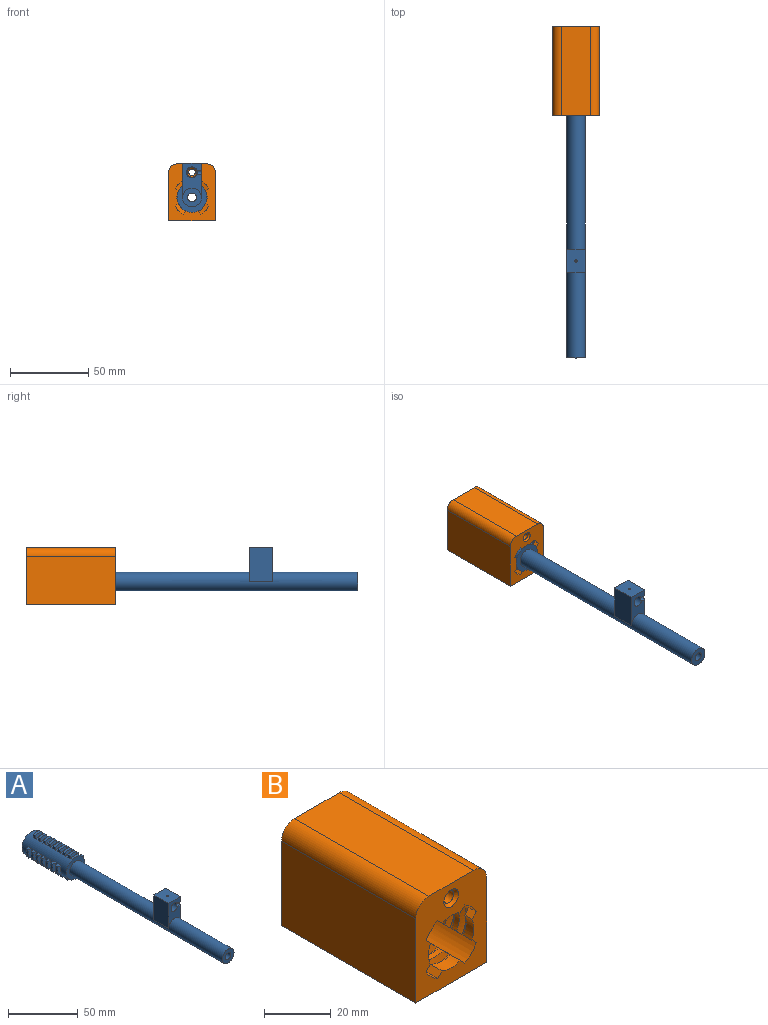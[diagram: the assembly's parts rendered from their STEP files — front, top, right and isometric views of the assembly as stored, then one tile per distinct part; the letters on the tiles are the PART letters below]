
ASSEMBLY  parts=2 mates=1
PART A: 166 faces, bbox 27.8x200.1x34.1 mm
  f0: cylinder r=9.5mm len=45mm, axis (0,1,0), area 2062.4mm2, adj f1,f2,f11,f12,f14,f15,f16,f17
  f1: plane 19x19mm, normal (0,1,0), area 169.7mm2, adj f0,f10
  f2: plane 19x19mm, normal (0,-1,0), area 170.4mm2, adj f0,f3
  f3: cylinder r=6mm len=155mm, axis (0,1,0), area 5560.6mm2, adj f2,f4,f156,f157,f160,f161
  f4: plane 12x12mm, normal (0,-1,0), area 87.6mm2, adj f3,f5
  f5: cylinder r=2.85mm len=157.2mm, axis (0,1,0), area 2815mm2, adj f4,f6
  f6: plane 6.43x6.43mm, normal (0,1,0), area 7mm2, adj f5,f7
  f7: cylinder r=3.21mm len=6.43mm, axis (0,1,0), area 104mm2, adj f6,f8
  f8: cone r=3.21mm half-angle=23deg, axis (0,1,0), area 79.8mm2, adj f7,f9
  f9: cone r=4.5mm half-angle=0.5deg, axis (0,1,0), area 974.5mm2, adj f8,f10
  f10: cone r=4.79mm half-angle=45deg, axis (0,1,0), area 59.1mm2, adj f1,f9
  f11: bspline ~20.78x7.25mm, area 18.4mm2, adj f0,f13,f14,f15
  f12: bspline ~20.78x7.25mm, area 18.4mm2, adj f0,f13,f14,f15
  f13: cylinder r=12mm len=7mm, axis (0,-1,0), area 14.2mm2, adj f11,f12,f14,f15
  f14: plane 3.1x2.75mm, normal (-1,0,0), area 6.6mm2, adj f0,f11,f12,f13
  f15: plane 3.1x2.75mm, normal (1,0,0), area 6.6mm2, adj f0,f11,f12,f13
  f16: bspline ~20.78x7.25mm, area 18.4mm2, adj f0,f18,f19,f20
  f17: bspline ~20.78x7.25mm, area 18.4mm2, adj f0,f18,f19,f20
  f18: cylinder r=12mm len=7mm, axis (0,-1,0), area 14.2mm2, adj f16,f17,f19,f20
  f19: plane 3.1x2.75mm, normal (-1,0,0), area 6.6mm2, adj f0,f16,f17,f18
  f20: plane 3.1x2.75mm, normal (1,0,0), area 6.6mm2, adj f0,f16,f17,f18
  f21: bspline ~20.78x7.25mm, area 18.4mm2, adj f0,f23,f24,f25
  f22: bspline ~20.78x7.25mm, area 18.4mm2, adj f0,f23,f24,f25
  f23: cylinder r=12mm len=7mm, axis (0,-1,0), area 14.2mm2, adj f21,f22,f24,f25
  f24: plane 3.1x2.75mm, normal (-1,0,0), area 6.6mm2, adj f0,f21,f22,f23
  f25: plane 3.1x2.75mm, normal (1,0,0), area 6.6mm2, adj f0,f21,f22,f23
  f26: bspline ~20.78x7.25mm, area 18.4mm2, adj f0,f28,f29,f30
  f27: bspline ~20.78x7.25mm, area 18.4mm2, adj f0,f28,f29,f30
  f28: cylinder r=12mm len=7mm, axis (0,-1,0), area 14.2mm2, adj f26,f27,f29,f30
  f29: plane 3.1x2.75mm, normal (-1,0,0), area 6.6mm2, adj f0,f26,f27,f28
  f30: plane 3.1x2.75mm, normal (1,0,0), area 6.6mm2, adj f0,f26,f27,f28
  f31: bspline ~20.78x7.25mm, area 18.4mm2, adj f0,f33,f34,f35
  f32: bspline ~20.78x7.25mm, area 18.4mm2, adj f0,f33,f34,f35
  f33: cylinder r=12mm len=7mm, axis (0,-1,0), area 14.2mm2, adj f31,f32,f34,f35
  f34: plane 3.1x2.75mm, normal (-1,0,0), area 6.6mm2, adj f0,f31,f32,f33
  f35: plane 3.1x2.75mm, normal (1,0,0), area 6.6mm2, adj f0,f31,f32,f33
  f36: bspline ~20.78x7.25mm, area 18.4mm2, adj f0,f38,f39,f40
  f37: bspline ~20.78x7.25mm, area 18.4mm2, adj f0,f38,f39,f40
  f38: cylinder r=12mm len=7mm, axis (0,-1,0), area 14.2mm2, adj f36,f37,f39,f40
  f39: plane 3.1x2.75mm, normal (-1,0,0), area 6.6mm2, adj f0,f36,f37,f38
  f40: plane 3.1x2.75mm, normal (1,0,0), area 6.6mm2, adj f0,f36,f37,f38
  f41: bspline ~20.78x7.25mm, area 18.4mm2, adj f0,f43,f44,f45
  f42: bspline ~20.78x7.25mm, area 18.4mm2, adj f0,f43,f44,f45
  f43: cylinder r=12mm len=7mm, axis (0,-1,0), area 14.2mm2, adj f41,f42,f44,f45
  f44: plane 3.1x2.75mm, normal (-1,0,0), area 6.6mm2, adj f0,f41,f42,f43
  f45: plane 3.1x2.75mm, normal (1,0,0), area 6.6mm2, adj f0,f41,f42,f43
  f46: bspline ~20.78x7.25mm, area 18.4mm2, adj f0,f48,f49,f50
  f47: bspline ~20.78x7.25mm, area 18.4mm2, adj f0,f48,f49,f50
  f48: cylinder r=12mm len=7mm, axis (0,-1,0), area 14.2mm2, adj f46,f47,f49,f50
  f49: plane 3.1x2.75mm, normal (-1,0,0), area 6.6mm2, adj f0,f46,f47,f48
  f50: plane 3.1x2.75mm, normal (1,0,0), area 6.6mm2, adj f0,f46,f47,f48
  f51: bspline ~20.78x7.25mm, area 18.4mm2, adj f0,f53,f54,f55
  f52: bspline ~20.78x7.25mm, area 18.4mm2, adj f0,f53,f54,f55
  f53: cylinder r=12mm len=7mm, axis (0,-1,0), area 14.2mm2, adj f51,f52,f54,f55
  f54: plane 3.1x2.75mm, normal (-1,0,0), area 6.6mm2, adj f0,f51,f52,f53
  f55: plane 3.1x2.75mm, normal (1,0,0), area 6.6mm2, adj f0,f51,f52,f53
  f56: bspline ~20.78x7.25mm, area 18.4mm2, adj f0,f58,f59,f60
  f57: bspline ~20.78x7.25mm, area 18.4mm2, adj f0,f58,f59,f60
  f58: cylinder r=12mm len=7mm, axis (0,-1,0), area 14.2mm2, adj f56,f57,f59,f60
  f59: plane 3.1x2.75mm, normal (-1,0,0), area 6.6mm2, adj f0,f56,f57,f58
  f60: plane 3.1x2.75mm, normal (1,0,0), area 6.6mm2, adj f0,f56,f57,f58
  f61: bspline ~20.78x7.25mm, area 18.4mm2, adj f0,f63,f64,f65
  f62: bspline ~20.78x7.25mm, area 18.4mm2, adj f0,f63,f64,f65
  f63: cylinder r=12mm len=7mm, axis (0,-1,0), area 14.2mm2, adj f61,f62,f64,f65
  f64: plane 3.1x2.75mm, normal (-1,0,0), area 6.6mm2, adj f0,f61,f62,f63
  f65: plane 3.1x2.75mm, normal (1,0,0), area 6.6mm2, adj f0,f61,f62,f63
  f66: bspline ~12x5.63mm, area 18.4mm2, adj f0,f68,f69,f70
  f67: bspline ~12x5.63mm, area 18.4mm2, adj f0,f68,f69,f70
  f68: cylinder r=12mm len=7mm, axis (0,-1,0), area 14.2mm2, adj f66,f67,f69,f70
  f69: plane 3.11x2.75mm, normal (0,0,-1), area 6.6mm2, adj f0,f66,f67,f68
  f70: plane 3.11x2.75mm, normal (0,0,1), area 6.6mm2, adj f0,f66,f67,f68
  f71: bspline ~20.78x7.25mm, area 18.4mm2, adj f0,f73,f74,f75
  f72: bspline ~20.78x7.25mm, area 18.4mm2, adj f0,f73,f74,f75
  f73: cylinder r=12mm len=7mm, axis (0,-1,0), area 14.2mm2, adj f71,f72,f74,f75
  f74: plane 3.1x2.75mm, normal (-1,0,0), area 6.6mm2, adj f0,f71,f72,f73
  f75: plane 3.1x2.75mm, normal (1,0,0), area 6.6mm2, adj f0,f71,f72,f73
  f76: bspline ~20.78x7.25mm, area 18.4mm2, adj f0,f78,f79,f80
  f77: bspline ~20.78x7.25mm, area 18.4mm2, adj f0,f78,f79,f80
  f78: cylinder r=12mm len=7mm, axis (0,-1,0), area 14.2mm2, adj f76,f77,f79,f80
  f79: plane 3.1x2.75mm, normal (-1,0,0), area 6.6mm2, adj f0,f76,f77,f78
  f80: plane 3.1x2.75mm, normal (1,0,0), area 6.6mm2, adj f0,f76,f77,f78
  f81: bspline ~12x5.63mm, area 18.4mm2, adj f0,f83,f84,f85
  f82: bspline ~12x5.63mm, area 18.4mm2, adj f0,f83,f84,f85
  f83: cylinder r=12mm len=7mm, axis (0,-1,0), area 14.2mm2, adj f81,f82,f84,f85
  f84: plane 3.11x2.75mm, normal (0,0,-1), area 6.6mm2, adj f0,f81,f82,f83
  f85: plane 3.11x2.75mm, normal (0,0,1), area 6.6mm2, adj f0,f81,f82,f83
  f86: bspline ~20.78x7.25mm, area 18.4mm2, adj f0,f88,f89,f90
  f87: bspline ~20.78x7.25mm, area 18.4mm2, adj f0,f88,f89,f90
  f88: cylinder r=12mm len=7mm, axis (0,-1,0), area 14.2mm2, adj f86,f87,f89,f90
  f89: plane 3.1x2.75mm, normal (-1,0,0), area 6.6mm2, adj f0,f86,f87,f88
  f90: plane 3.1x2.75mm, normal (1,0,0), area 6.6mm2, adj f0,f86,f87,f88
  f91: bspline ~12x5.63mm, area 18.4mm2, adj f0,f93,f94,f95
  f92: bspline ~12x5.63mm, area 18.4mm2, adj f0,f93,f94,f95
  f93: cylinder r=12mm len=7mm, axis (0,-1,0), area 14.2mm2, adj f91,f92,f94,f95
  f94: plane 3.11x2.75mm, normal (0,0,-1), area 6.6mm2, adj f0,f91,f92,f93
  f95: plane 3.11x2.75mm, normal (0,0,1), area 6.6mm2, adj f0,f91,f92,f93
  f96: bspline ~20.78x7.25mm, area 18.4mm2, adj f0,f98,f99,f100
  f97: bspline ~20.78x7.25mm, area 18.4mm2, adj f0,f98,f99,f100
  f98: cylinder r=12mm len=7mm, axis (0,-1,0), area 14.2mm2, adj f96,f97,f99,f100
  f99: plane 3.1x2.75mm, normal (-1,0,0), area 6.6mm2, adj f0,f96,f97,f98
  f100: plane 3.1x2.75mm, normal (1,0,0), area 6.6mm2, adj f0,f96,f97,f98
  f101: bspline ~12x5.63mm, area 18.4mm2, adj f0,f103,f104,f105
  f102: bspline ~12x5.63mm, area 18.4mm2, adj f0,f103,f104,f105
  f103: cylinder r=12mm len=7mm, axis (0,-1,0), area 14.2mm2, adj f101,f102,f104,f105
  f104: plane 3.11x2.75mm, normal (0,0,-1), area 6.6mm2, adj f0,f101,f102,f103
  f105: plane 3.11x2.75mm, normal (0,0,1), area 6.6mm2, adj f0,f101,f102,f103
  f106: bspline ~12x5.63mm, area 18.4mm2, adj f0,f108,f109,f110
  f107: bspline ~12x5.63mm, area 18.4mm2, adj f0,f108,f109,f110
  f108: cylinder r=12mm len=7mm, axis (0,-1,0), area 14.2mm2, adj f106,f107,f109,f110
  f109: plane 3.11x2.75mm, normal (0,0,-1), area 6.6mm2, adj f0,f106,f107,f108
  f110: plane 3.11x2.75mm, normal (0,0,1), area 6.6mm2, adj f0,f106,f107,f108
  f111: bspline ~12x5.63mm, area 18.4mm2, adj f0,f113,f114,f115
  f112: bspline ~12x5.63mm, area 18.4mm2, adj f0,f113,f114,f115
  f113: cylinder r=12mm len=7mm, axis (0,-1,0), area 14.2mm2, adj f111,f112,f114,f115
  f114: plane 3.11x2.75mm, normal (0,0,-1), area 6.6mm2, adj f0,f111,f112,f113
  f115: plane 3.11x2.75mm, normal (0,0,1), area 6.6mm2, adj f0,f111,f112,f113
  f116: bspline ~12x5.63mm, area 18.4mm2, adj f0,f118,f119,f120
  f117: bspline ~12x5.63mm, area 18.4mm2, adj f0,f118,f119,f120
  f118: cylinder r=12mm len=7mm, axis (0,-1,0), area 14.2mm2, adj f116,f117,f119,f120
  f119: plane 3.11x2.75mm, normal (0,0,-1), area 6.6mm2, adj f0,f116,f117,f118
  f120: plane 3.11x2.75mm, normal (0,0,1), area 6.6mm2, adj f0,f116,f117,f118
  f121: bspline ~12x5.63mm, area 18.4mm2, adj f0,f123,f124,f125
  f122: bspline ~12x5.63mm, area 18.4mm2, adj f0,f123,f124,f125
  f123: cylinder r=12mm len=7mm, axis (0,-1,0), area 14.2mm2, adj f121,f122,f124,f125
  f124: plane 3.11x2.75mm, normal (0,0,1), area 6.6mm2, adj f0,f121,f122,f123
  f125: plane 3.11x2.75mm, normal (0,0,-1), area 6.6mm2, adj f0,f121,f122,f123
  f126: bspline ~12x5.63mm, area 18.4mm2, adj f0,f128,f129,f130
  f127: bspline ~12x5.63mm, area 18.4mm2, adj f0,f128,f129,f130
  f128: cylinder r=12mm len=7mm, axis (0,-1,0), area 14.2mm2, adj f126,f127,f129,f130
  f129: plane 3.11x2.75mm, normal (0,0,1), area 6.6mm2, adj f0,f126,f127,f128
  f130: plane 3.11x2.75mm, normal (0,0,-1), area 6.6mm2, adj f0,f126,f127,f128
  f131: bspline ~12x5.63mm, area 18.4mm2, adj f0,f133,f134,f135
  f132: bspline ~12x5.63mm, area 18.4mm2, adj f0,f133,f134,f135
  f133: cylinder r=12mm len=7mm, axis (0,-1,0), area 14.2mm2, adj f131,f132,f134,f135
  f134: plane 3.11x2.75mm, normal (0,0,1), area 6.6mm2, adj f0,f131,f132,f133
  f135: plane 3.11x2.75mm, normal (0,0,-1), area 6.6mm2, adj f0,f131,f132,f133
  f136: bspline ~12x5.63mm, area 18.4mm2, adj f0,f138,f139,f140
  f137: bspline ~12x5.63mm, area 18.4mm2, adj f0,f138,f139,f140
  f138: cylinder r=12mm len=7mm, axis (0,-1,0), area 14.2mm2, adj f136,f137,f139,f140
  f139: plane 3.11x2.75mm, normal (0,0,1), area 6.6mm2, adj f0,f136,f137,f138
  f140: plane 3.11x2.75mm, normal (0,0,-1), area 6.6mm2, adj f0,f136,f137,f138
  f141: bspline ~12x5.63mm, area 18.4mm2, adj f0,f143,f144,f145
  f142: bspline ~12x5.63mm, area 18.4mm2, adj f0,f143,f144,f145
  f143: cylinder r=12mm len=7mm, axis (0,-1,0), area 14.2mm2, adj f141,f142,f144,f145
  f144: plane 3.11x2.75mm, normal (0,0,1), area 6.6mm2, adj f0,f141,f142,f143
  f145: plane 3.11x2.75mm, normal (0,0,-1), area 6.6mm2, adj f0,f141,f142,f143
  f146: bspline ~12x5.63mm, area 18.4mm2, adj f0,f148,f149,f150
  f147: bspline ~12x5.63mm, area 18.4mm2, adj f0,f148,f149,f150
  f148: cylinder r=12mm len=7mm, axis (0,-1,0), area 14.2mm2, adj f146,f147,f149,f150
  f149: plane 3.11x2.75mm, normal (0,0,1), area 6.6mm2, adj f0,f146,f147,f148
  f150: plane 3.11x2.75mm, normal (0,0,-1), area 6.6mm2, adj f0,f146,f147,f148
  f151: bspline ~12x5.63mm, area 18.4mm2, adj f0,f153,f154,f155
  f152: bspline ~12x5.63mm, area 18.4mm2, adj f0,f153,f154,f155
  f153: cylinder r=12mm len=7mm, axis (0,-1,0), area 14.2mm2, adj f151,f152,f154,f155
  f154: plane 3.11x2.75mm, normal (0,0,1), area 6.6mm2, adj f0,f151,f152,f153
  f155: plane 3.11x2.75mm, normal (0,0,-1), area 6.6mm2, adj f0,f151,f152,f153
  f156: plane 22x15mm, normal (-1,0,0), area 330mm2, adj f3,f158,f160,f161
  f157: plane 22x15mm, normal (1,0,0), area 326.5mm2, adj f3,f158,f160,f161,f165
  f158: plane 15x12mm, normal (0,0,1), area 178.2mm2, adj f156,f157,f160,f161,f162
  f159: cylinder r=3.5mm len=15mm, axis (0,-1,0), area 322.7mm2, adj f160,f161,f162,f163,f165
  f160: plane 22x12mm, normal (0,1,0), area 169mm2, adj f3,f156,f157,f158,f159
  f161: plane 22x12mm, normal (0,-1,0), area 161.1mm2, adj f3,f156,f157,f158,f159,f165
  f162: cylinder r=0.75mm len=2.58mm, axis (0,0,1), area 12.2mm2, adj f158,f159
  f163: cylinder r=0.75mm len=6.58mm, axis (0,0,1), area 30.7mm2, adj f159,f164
  f164: plane 1.5x1.5mm, normal (0,0,1), area 1.8mm2, adj f163
  f165: cylinder r=1.5mm len=3mm, axis (1,0,0), area 12.6mm2, adj f157,f159,f161
PART B: 198 faces, bbox 30.3x57.3x36.8 mm
  f0: bspline ~20.96x7.35mm, area 25.1mm2, adj f72,f101,f119,f167
  f1: bspline ~20.96x7.35mm, area 25.1mm2, adj f72,f99,f118,f168
  f2: bspline ~20.96x7.35mm, area 25.1mm2, adj f72,f106,f114,f170
  f3: bspline ~20.96x7.35mm, area 25.1mm2, adj f72,f103,f112,f171
  f4: bspline ~20.96x7.35mm, area 25.1mm2, adj f72,f85,f129,f158
  f5: bspline ~20.96x7.35mm, area 25.1mm2, adj f72,f83,f127,f160
  f6: bspline ~20.96x7.35mm, area 25.1mm2, adj f72,f90,f123,f164
  f7: bspline ~20.96x7.35mm, area 25.1mm2, adj f72,f91,f121,f166
  f8: bspline ~12.1x5.74mm, area 25.1mm2, adj f72,f78,f105,f174
  f9: bspline ~12.1x5.74mm, area 25.1mm2, adj f72,f88,f104,f175
  f10: bspline ~12.1x5.74mm, area 25.1mm2, adj f72,f86,f102,f176
  f11: bspline ~12.1x5.74mm, area 25.1mm2, adj f72,f84,f100,f177
  f12: bspline ~20.96x7.35mm, area 25.1mm2, adj f72,f97,f110,f172
  f13: bspline ~20.96x7.35mm, area 25.1mm2, adj f72,f95,f108,f173
  f14: bspline ~12.1x5.74mm, area 25.1mm2, adj f72,f84,f100,f177
  f15: bspline ~12.1x5.74mm, area 25.1mm2, adj f72,f82,f98,f178
  f16: bspline ~20.96x7.35mm, area 25.1mm2, adj f72,f95,f108,f173
  f17: bspline ~20.96x7.35mm, area 25.1mm2, adj f72,f93,f116,f169
  f18: bspline ~20.96x7.35mm, area 25.1mm2, adj f72,f87,f131,f156
  f19: bspline ~20.96x7.35mm, area 25.1mm2, adj f72,f85,f129,f158
  f20: bspline ~20.96x7.35mm, area 25.1mm2, adj f72,f75,f76,f150
  f21: bspline ~20.96x7.35mm, area 25.1mm2, adj f72,f106,f114,f170
  f22: bspline ~20.96x7.35mm, area 25.1mm2, adj f72,f89,f134,f153
  f23: bspline ~20.96x7.35mm, area 25.1mm2, adj f72,f87,f131,f156
  f24: bspline ~12.1x5.74mm, area 25.1mm2, adj f72,f75,f77,f150
  f25: bspline ~12.1x5.74mm, area 25.1mm2, adj f72,f78,f105,f174
  f26: bspline ~20.96x7.35mm, area 25.1mm2, adj f72,f74,f79,f150,f151
  f27: bspline ~20.96x7.35mm, area 25.1mm2, adj f72,f89,f134,f153
  f28: bspline ~20.96x7.35mm, area 25.1mm2, adj f72,f81,f125,f162
  f29: bspline ~20.96x7.35mm, area 25.1mm2, adj f72,f90,f123,f164
  f30: bspline ~20.96x7.35mm, area 25.1mm2, adj f72,f73,f77,f150
  f31: bspline ~11.43x3.64mm, area 25.1mm2, adj f72,f73,f79,f150,f151
  f32: bspline ~20.96x7.35mm, area 25.1mm2, adj f72,f103,f112,f171
  f33: bspline ~20.96x7.35mm, area 25.1mm2, adj f72,f101,f119,f167
  f34: bspline ~12.1x5.74mm, area 25.1mm2, adj f72,f88,f104,f175
  f35: bspline ~12.1x5.74mm, area 25.1mm2, adj f72,f86,f102,f176
  f36: bspline ~12.1x5.74mm, area 25.1mm2, adj f72,f80,f96,f179
  f37: bspline ~12.1x5.74mm, area 25.1mm2, adj f72,f92,f94,f180
  f38: bspline ~12.1x5.74mm, area 25.1mm2, adj f72,f82,f98,f178
  f39: bspline ~12.1x5.74mm, area 25.1mm2, adj f72,f80,f96,f179
  f40: bspline ~20.96x7.35mm, area 25.1mm2, adj f72,f83,f127,f160
  f41: bspline ~20.96x7.35mm, area 25.1mm2, adj f72,f81,f125,f162
  f42: bspline ~20.96x7.35mm, area 25.1mm2, adj f72,f99,f118,f168
  f43: bspline ~20.96x7.35mm, area 25.1mm2, adj f72,f97,f110,f172
  f44: bspline ~12.1x5.74mm, area 25.1mm2, adj f72,f113,f133,f154
  f45: bspline ~12.1x5.74mm, area 25.1mm2, adj f72,f111,f132,f155
  f46: bspline ~12.1x5.74mm, area 25.1mm2, adj f72,f107,f124,f163
  f47: bspline ~12.1x5.74mm, area 25.1mm2, adj f72,f115,f122,f165
  f48: bspline ~12.1x5.74mm, area 25.1mm2, adj f72,f109,f126,f161
  f49: bspline ~12.1x5.74mm, area 25.1mm2, adj f72,f107,f124,f163
  f50: bspline ~12.1x5.74mm, area 25.1mm2, adj f72,f117,f128,f159
  f51: bspline ~12.1x5.74mm, area 25.1mm2, adj f72,f109,f126,f161
  f52: bspline ~12.1x5.74mm, area 25.1mm2, adj f72,f120,f130,f157
  f53: bspline ~12.1x5.74mm, area 25.1mm2, adj f72,f117,f128,f159
  f54: bspline ~12.1x5.74mm, area 25.1mm2, adj f72,f111,f132,f155
  f55: bspline ~12.1x5.74mm, area 25.1mm2, adj f72,f120,f130,f157
  f56: bspline ~12.1x5.74mm, area 25.1mm2, adj f72,f74,f76,f150
  f57: bspline ~12.1x5.74mm, area 25.1mm2, adj f72,f113,f133,f154
  f58: plane 36.5x30mm, normal (0,1,0), area 799.2mm2, adj f67,f68,f69,f70,f135,f136,f137,f138
  f59: plane 5.46x3.28mm, normal (0,-1,0), area 13.4mm2, adj f147,f150,f152,f187
  f60: plane 5.06x5.06mm, normal (0,-1,0), area 13.4mm2, adj f145,f148,f150,f188
  f61: plane 5.46x3.28mm, normal (0,-1,0), area 13.4mm2, adj f143,f146,f150,f181
  f62: plane 5.06x5.06mm, normal (0,-1,0), area 13.4mm2, adj f142,f144,f150,f182
  f63: plane 5.46x3.28mm, normal (0,-1,0), area 13.4mm2, adj f139,f141,f150,f183
  f64: plane 5.06x5.06mm, normal (0,-1,0), area 13.4mm2, adj f138,f140,f150,f184
  f65: plane 5.46x3.28mm, normal (0,-1,0), area 13.4mm2, adj f135,f137,f150,f185
  f66: plane 5.06x5.06mm, normal (0,-1,0), area 13.4mm2, adj f136,f149,f150,f186
  f67: plane 57x31mm, normal (1,0,0), area 1767mm2, adj f58,f70,f71,f193
  f68: plane 57x19mm, normal (0,0,1), area 1083mm2, adj f58,f71,f193,f194
  f69: plane 57x31mm, normal (-1,0,0), area 1767mm2, adj f58,f70,f71,f194
  f70: plane 57x30mm, normal (0,0,-1), area 1710mm2, adj f58,f67,f69,f71
  f71: plane 36.5x30mm, normal (0,-1,0), area 691mm2, adj f67,f68,f69,f70,f72,f91,f92,f93
  f72: cylinder r=12.1mm len=39.89mm, axis (0,-1,0), area 1741.4mm2, adj f0,f1,f2,f3,f4,f5,f6,f7
  f73: plane 3.06x1.97mm, normal (-0.71,0,0.71), area 6.6mm2, adj f30,f31,f72,f150
  f74: bspline ~17.79x14.94mm, area 18.4mm2, adj f26,f56,f72,f150
  f75: bspline ~17.79x14.94mm, area 18.4mm2, adj f20,f24,f72,f150
  f76: bspline ~18.96x13.92mm, area 18.4mm2, adj f20,f56,f72,f150
  f77: bspline ~18.96x13.92mm, area 18.4mm2, adj f24,f30,f72,f150
  f78: plane 3.29x2.16mm, normal (0.71,0,0.71), area 6.7mm2, adj f8,f25,f72,f174
  f79: plane 3.17x2.04mm, normal (-0.71,0,-0.71), area 6.6mm2, adj f26,f31,f72,f151
  f80: plane 3.29x2.16mm, normal (0.71,0,0.71), area 6.7mm2, adj f36,f39,f72,f179
  f81: plane 3.17x2.04mm, normal (-0.71,0,-0.71), area 6.6mm2, adj f28,f41,f72,f162
  f82: plane 3.29x2.16mm, normal (0.71,0,0.71), area 6.7mm2, adj f15,f38,f72,f178
  f83: plane 3.17x2.04mm, normal (-0.71,0,-0.71), area 6.6mm2, adj f5,f40,f72,f160
  f84: plane 3.29x2.16mm, normal (0.71,0,0.71), area 6.7mm2, adj f11,f14,f72,f177
  f85: plane 3.17x2.04mm, normal (-0.71,0,-0.71), area 6.6mm2, adj f4,f19,f72,f158
  f86: plane 3.29x2.16mm, normal (0.71,0,0.71), area 6.7mm2, adj f10,f35,f72,f176
  f87: plane 3.17x2.04mm, normal (-0.71,0,-0.71), area 6.6mm2, adj f18,f23,f72,f156
  f88: plane 3.29x2.16mm, normal (0.71,0,0.71), area 6.7mm2, adj f9,f34,f72,f175
  f89: plane 3.17x2.04mm, normal (-0.71,0,-0.71), area 6.6mm2, adj f22,f27,f72,f153
  f90: plane 3.17x2.04mm, normal (-0.71,0,-0.71), area 6.7mm2, adj f6,f29,f72,f164
  f91: plane 2.21x1.97mm, normal (-0.71,0,-0.71), area 5mm2, adj f7,f71,f72,f166
  f92: plane 6.74x1.97mm, normal (0.71,0,0.71), area 16.9mm2, adj f37,f71,f72,f180
  f93: plane 5.5x1.97mm, normal (-0.71,0,0.71), area 13.5mm2, adj f17,f71,f72,f169
  f94: plane 6.02x2.03mm, normal (0.71,0,-0.71), area 14.9mm2, adj f37,f71,f72,f180
  f95: plane 3.16x2.03mm, normal (-0.71,0,0.71), area 6.6mm2, adj f13,f16,f72,f173
  f96: plane 3.17x2.03mm, normal (0.71,0,-0.71), area 6.6mm2, adj f36,f39,f72,f179
  f97: plane 3.16x2.03mm, normal (-0.71,0,0.71), area 6.6mm2, adj f12,f43,f72,f172
  f98: plane 3.17x2.03mm, normal (0.71,0,-0.71), area 6.6mm2, adj f15,f38,f72,f178
  f99: plane 3.16x2.03mm, normal (-0.71,0,0.71), area 6.6mm2, adj f1,f42,f72,f168
  f100: plane 3.17x2.03mm, normal (0.71,0,-0.71), area 6.6mm2, adj f11,f14,f72,f177
  f101: plane 3.16x2.03mm, normal (-0.71,0,0.71), area 6.6mm2, adj f0,f33,f72,f167
  f102: plane 3.17x2.03mm, normal (0.71,0,-0.71), area 6.6mm2, adj f10,f35,f72,f176
  f103: plane 3.16x2.03mm, normal (-0.71,0,0.71), area 6.6mm2, adj f3,f32,f72,f171
  f104: plane 3.17x2.03mm, normal (0.71,0,-0.71), area 6.6mm2, adj f9,f34,f72,f175
  f105: plane 3.17x2.03mm, normal (0.71,0,-0.71), area 6.6mm2, adj f8,f25,f72,f174
  f106: plane 3.16x2.03mm, normal (-0.71,0,0.71), area 6.6mm2, adj f2,f21,f72,f170
  f107: plane 3.29x2.16mm, normal (-0.71,0,-0.71), area 6.7mm2, adj f46,f49,f72,f163
  f108: plane 3.17x2.04mm, normal (0.71,0,0.71), area 6.6mm2, adj f13,f16,f72,f173
  f109: plane 3.29x2.16mm, normal (-0.71,0,-0.71), area 6.7mm2, adj f48,f51,f72,f161
  f110: plane 3.17x2.04mm, normal (0.71,0,0.71), area 6.6mm2, adj f12,f43,f72,f172
  f111: plane 3.29x2.16mm, normal (-0.71,0,-0.71), area 6.7mm2, adj f45,f54,f72,f155
  f112: plane 3.17x2.04mm, normal (0.71,0,0.71), area 6.6mm2, adj f3,f32,f72,f171
  f113: plane 3.29x2.16mm, normal (-0.71,0,-0.71), area 6.7mm2, adj f44,f57,f72,f154
  f114: plane 3.17x2.04mm, normal (0.71,0,0.71), area 6.6mm2, adj f2,f21,f72,f170
  f115: plane 4.24x1.97mm, normal (-0.71,0,-0.71), area 10.2mm2, adj f47,f71,f72,f165
  f116: plane 4.78x2.04mm, normal (0.71,0,0.71), area 11.6mm2, adj f17,f71,f72,f169
  f117: plane 3.29x2.16mm, normal (-0.71,0,-0.71), area 6.7mm2, adj f50,f53,f72,f159
  f118: plane 3.17x2.04mm, normal (0.71,0,0.71), area 6.6mm2, adj f1,f42,f72,f168
  f119: plane 3.17x2.04mm, normal (0.71,0,0.71), area 6.6mm2, adj f0,f33,f72,f167
  f120: plane 3.29x2.16mm, normal (-0.71,0,-0.71), area 6.7mm2, adj f52,f55,f72,f157
  f121: plane 3x1.97mm, normal (0.71,0,-0.71), area 6.9mm2, adj f7,f71,f72,f166
  f122: plane 3.52x2.03mm, normal (-0.71,0,0.71), area 8.3mm2, adj f47,f71,f72,f165
  f123: plane 3.16x2.03mm, normal (0.71,0,-0.71), area 6.6mm2, adj f6,f29,f72,f164
  f124: plane 3.17x2.03mm, normal (-0.71,0,0.71), area 6.6mm2, adj f46,f49,f72,f163
  f125: plane 3.16x2.03mm, normal (0.71,0,-0.71), area 6.6mm2, adj f28,f41,f72,f162
  f126: plane 3.17x2.04mm, normal (-0.71,0,0.71), area 6.7mm2, adj f48,f51,f72,f161
  f127: plane 3.17x2.03mm, normal (0.71,0,-0.71), area 6.6mm2, adj f5,f40,f72,f160
  f128: plane 3.16x2.03mm, normal (-0.71,0,0.71), area 6.6mm2, adj f50,f53,f72,f159
  f129: plane 3.16x2.03mm, normal (0.71,0,-0.71), area 6.6mm2, adj f4,f19,f72,f158
  f130: plane 3.17x2.03mm, normal (-0.71,0,0.71), area 6.6mm2, adj f52,f55,f72,f157
  f131: plane 3.16x2.03mm, normal (0.71,0,-0.71), area 6.6mm2, adj f18,f23,f72,f156
  f132: plane 3.17x2.03mm, normal (-0.71,0,0.71), area 6.6mm2, adj f45,f54,f72,f155
  f133: plane 3.17x2.03mm, normal (-0.71,0,0.71), area 6.6mm2, adj f44,f57,f72,f154
  f134: plane 3.16x2.03mm, normal (0.71,0,-0.71), area 6.6mm2, adj f22,f27,f72,f153
  f135: plane 6.01x2.9mm, normal (0.92,0,-0.38), area 15.7mm2, adj f58,f65,f150,f185
  f136: plane 6.01x2.9mm, normal (-0.92,0,0.38), area 15.7mm2, adj f58,f66,f150,f186
  f137: plane 6.01x2.9mm, normal (-0.92,0,-0.38), area 15.7mm2, adj f58,f65,f150,f185
  f138: plane 6.01x2.9mm, normal (0.92,0,0.38), area 15.7mm2, adj f58,f64,f150,f184
  f139: plane 6.01x2.9mm, normal (0.38,0,0.92), area 15.7mm2, adj f58,f63,f150,f183
  f140: plane 6.01x2.9mm, normal (-0.38,0,-0.92), area 15.7mm2, adj f58,f64,f150,f184
  f141: plane 6.01x2.9mm, normal (0.38,0,-0.92), area 15.7mm2, adj f58,f63,f150,f183
  f142: plane 6.01x2.9mm, normal (-0.38,0,0.92), area 15.7mm2, adj f58,f62,f150,f182
  f143: plane 6.01x2.9mm, normal (-0.92,0,0.38), area 15.7mm2, adj f58,f61,f150,f181
  f144: plane 6.01x2.9mm, normal (0.92,0,-0.38), area 15.7mm2, adj f58,f62,f150,f182
  f145: plane 6.01x2.9mm, normal (-0.92,0,-0.38), area 15.7mm2, adj f58,f60,f150,f188
  f146: plane 6.01x2.9mm, normal (0.92,0,0.38), area 15.7mm2, adj f58,f61,f150,f181
  f147: plane 6.01x2.9mm, normal (-0.38,0,-0.92), area 15.7mm2, adj f58,f59,f150,f187
  f148: plane 6.01x2.9mm, normal (0.38,0,0.92), area 15.7mm2, adj f58,f60,f150,f188
  f149: plane 6.01x2.9mm, normal (0.38,0,-0.92), area 15.7mm2, adj f58,f66,f150,f186
  f150: cylinder r=9.6mm len=22.24mm, axis (0,1,0), area 905.5mm2, adj f20,f24,f26,f30,f31,f56,f58,f59
  f151: cylinder r=9.6mm len=2.14mm, axis (0,1,0), area 2.4mm2, adj f26,f31,f79,f150
  f152: plane 6.01x2.9mm, normal (-0.38,0,0.92), area 15.7mm2, adj f58,f59,f150,f187
  f153: cylinder r=9.6mm len=7.69mm, axis (0,-1,0), area 16.1mm2, adj f22,f27,f89,f134
  f154: cylinder r=9.6mm len=7.69mm, axis (0,-1,0), area 16.1mm2, adj f44,f57,f113,f133
  f155: cylinder r=9.6mm len=7.69mm, axis (0,-1,0), area 16.1mm2, adj f45,f54,f111,f132
  f156: cylinder r=9.6mm len=7.69mm, axis (0,-1,0), area 16.1mm2, adj f18,f23,f87,f131
  f157: cylinder r=9.6mm len=7.69mm, axis (0,-1,0), area 16.1mm2, adj f52,f55,f120,f130
  f158: cylinder r=9.6mm len=7.69mm, axis (0,-1,0), area 16.1mm2, adj f4,f19,f85,f129
  f159: cylinder r=9.6mm len=7.69mm, axis (0,-1,0), area 16.1mm2, adj f50,f53,f117,f128
  f160: cylinder r=9.6mm len=7.69mm, axis (0,-1,0), area 16.1mm2, adj f5,f40,f83,f127
  f161: cylinder r=9.6mm len=7.69mm, axis (0,-1,0), area 16.1mm2, adj f48,f51,f109,f126
  f162: cylinder r=9.6mm len=7.69mm, axis (0,-1,0), area 16.1mm2, adj f28,f41,f81,f125
  f163: cylinder r=9.6mm len=7.69mm, axis (0,-1,0), area 16.1mm2, adj f46,f49,f107,f124
  f164: cylinder r=9.6mm len=7.69mm, axis (0,-1,0), area 16.1mm2, adj f6,f29,f90,f123
  f165: cylinder r=9.6mm len=7.69mm, axis (0,-1,0), area 25.9mm2, adj f47,f71,f115,f122
  f166: cylinder r=9.6mm len=7.69mm, axis (0,-1,0), area 16mm2, adj f7,f71,f91,f121
  f167: cylinder r=9.6mm len=7.69mm, axis (0,-1,0), area 16.1mm2, adj f0,f33,f101,f119
  f168: cylinder r=9.6mm len=7.69mm, axis (0,-1,0), area 16.1mm2, adj f1,f42,f99,f118
  f169: cylinder r=9.6mm len=7.69mm, axis (0,-1,0), area 35.8mm2, adj f17,f71,f93,f116
  f170: cylinder r=9.6mm len=7.69mm, axis (0,-1,0), area 16.1mm2, adj f2,f21,f106,f114
  f171: cylinder r=9.6mm len=7.69mm, axis (0,-1,0), area 16.1mm2, adj f3,f32,f103,f112
  f172: cylinder r=9.6mm len=7.69mm, axis (0,-1,0), area 16.1mm2, adj f12,f43,f97,f110
  f173: cylinder r=9.6mm len=7.69mm, axis (0,-1,0), area 16.1mm2, adj f13,f16,f95,f108
  f174: cylinder r=9.6mm len=7.69mm, axis (0,-1,0), area 16.1mm2, adj f8,f25,f78,f105
  f175: cylinder r=9.6mm len=7.69mm, axis (0,-1,0), area 16.1mm2, adj f9,f34,f88,f104
  f176: cylinder r=9.6mm len=7.69mm, axis (0,-1,0), area 16.1mm2, adj f10,f35,f86,f102
  f177: cylinder r=9.6mm len=7.69mm, axis (0,-1,0), area 16.1mm2, adj f11,f14,f84,f100
  f178: cylinder r=9.6mm len=7.69mm, axis (0,-1,0), area 16.1mm2, adj f15,f38,f82,f98
  f179: cylinder r=9.6mm len=7.69mm, axis (0,-1,0), area 16.1mm2, adj f36,f39,f80,f96
  f180: cylinder r=9.6mm len=7.69mm, axis (0,-1,0), area 45.7mm2, adj f37,f71,f92,f94
  f181: cone r=6.5mm half-angle=9.5deg, axis (0,1,0), area 21.2mm2, adj f58,f61,f143,f146
  f182: cone r=6.5mm half-angle=9.5deg, axis (0,1,0), area 21.2mm2, adj f58,f62,f142,f144
  f183: cone r=6.5mm half-angle=9.5deg, axis (0,1,0), area 21.2mm2, adj f58,f63,f139,f141
  f184: cone r=6.5mm half-angle=9.5deg, axis (0,1,0), area 21.2mm2, adj f58,f64,f138,f140
  f185: cone r=6.5mm half-angle=9.5deg, axis (0,1,0), area 21.2mm2, adj f58,f65,f135,f137
  f186: cone r=6.5mm half-angle=9.5deg, axis (0,1,0), area 21.2mm2, adj f58,f66,f136,f149
  f187: cone r=6.5mm half-angle=9.5deg, axis (0,1,0), area 21.2mm2, adj f58,f59,f147,f152
  f188: cone r=6.5mm half-angle=9.5deg, axis (0,1,0), area 21.2mm2, adj f58,f60,f145,f148
  f189: cylinder r=2.57mm len=15mm, axis (0,1,0), area 242.5mm2, adj f58,f190
  f190: plane 5.15x5.15mm, normal (0,1,0), area 20.8mm2, adj f189
  f191: cylinder r=2.61mm len=15mm, axis (0,1,0), area 246.3mm2, adj f58,f192
  f192: plane 5.23x5.23mm, normal (0,1,0), area 21.5mm2, adj f191
  f193: cylinder r=5.5mm len=57mm, axis (0,-1,0), area 492.4mm2, adj f58,f67,f68,f71
  f194: cylinder r=5.5mm len=57mm, axis (0,1,0), area 492.4mm2, adj f58,f68,f69,f71
  f195: cylinder r=2.1mm len=55mm, axis (0,1,0), area 725.7mm2, adj f196,f197
  f196: cone r=3.1mm half-angle=45deg, axis (0,-1,0), area 23.1mm2, adj f71,f195
  f197: cone r=2.1mm half-angle=45deg, axis (0,1,0), area 23.1mm2, adj f58,f195
PLACE A t=(0.05,16.45,-0.43)mm
PLACE B t=(0.05,16.45,-0.43)mm fixed
MATE cylindrical A.f0 <-> B.f153  axis (0,-1,0) through (0.05,-28.55,-0.43)mm
